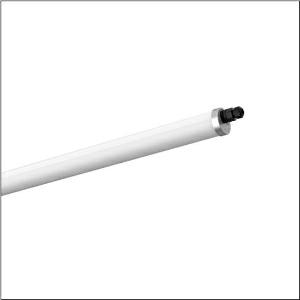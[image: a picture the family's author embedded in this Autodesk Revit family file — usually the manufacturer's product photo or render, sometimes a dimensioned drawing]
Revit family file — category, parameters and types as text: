
# Revit family: monsun_r__31_tube_51ft107n480a_b45d
name_source: partatom
category: Lighting Fixtures
units: mm (PartAtom-declared; Revit-internal decimal feet)

## family parameters
Cut with Voids When Loaded = No
Host = Face
Light Source = No
Part Type = Normal
Room Calculation Point = No
Round Connector Dimension = Use Diameter
Shared = No

## types (1)
- Monsun® 31 Tube (1 x LED, 8000 lm, 50 W, 4000K)
    Apparent Load = 50 VA
    CIE Flux Codes = 42 71 89 91 100
    Color Rendering = 80
    Color Temperature = 4000K
    Default Elevation = 1800 mm
    Description = Monsun® 31 Tube, tubular luminaire, primary optical cover: diffuser, of PMMA, light emission: direct distribution, primary light characteristic: symmetric, installation type: suspended mounting, surface-mounted, LED, rated luminous flux: 8.000lm, luminous efficacy: 160lm/W, light colour: 840, colour temperature: 4000K, with with 1 terminal, 3-pole, max. 2.5mm², through-wiring: 3x 1.5mm², mains connection: 220..240V, AC, 50/60Hz, rated input power: 50W, housing, cylindrical, of PMMA, semi-transparent, matt white, with luminaire and ceiling fastening, V4A, mounting with brackets of stainless steel, length: 1.560mm, diameter: 75mm, end cap, of stainless steel (V4A), protection rating (complete): IP67/IP69K, insulation class (complete): insulation class I (protective earthing), certification: CE, UKCA, impact resistance: IK07, permissible operating ambient temperature: -20..+40°C, corresponds to IFS (International Featured Standards) requirements for safety and quality in the food industry, usage in unprotected outdoor area possible with horizontal mounting, contact your sales advisor before using the luminaires in applications with unclear chemical exposure, large temperature fluctuations or condensation-forming humidity, packaging unit: 1 piece
    Height = 83 mm
    Lamp = 1 x LED
    Lamp Light Flux = 8000 lm
    Lamp Power = 50 W
    Lamp count = 1
    Length = 1560 mm
    Luminous efficacy = 160 lm/W
    Manufacturer = Siteco
    ModVariant = No
    Model = 51FT107N480A
    Mounting Place = Ceiling
    Mounting Type = Pendant
    Number of Poles = 1
    OnlyDefault = Yes
    Power Factor = 1
    Product Name = Monsun® 31 Tube
    Product group = tubular luminaire
    ProductGroupID = 906
    Protection Class = Protection class I
    RLX_Detail_Level = 1
    RLX_Emergency_Light_Flux = 0 lm
    RLX_Emergency_Type = 0
    RLX_Emergency_Type_DB = No
    RlxData = <blob elided: 25329 chars, md5=a1f534ec>
    Socket = socket
    Standby Power = 0 W
    System Light Flux = 8000 lm
    System Power = 50 W
    Type Comments = Product without accessories
    Type Image = l_1228461.jpg
    URL = http://relux.com
    VarID = ---
    Voltage = 0 V
    Weight = 0.00 kg
    Width = 75 mm

## geometry (parser evidence)
native form markers: Blend x4, Sweep x14
no freeform markers — native parametric forms only
